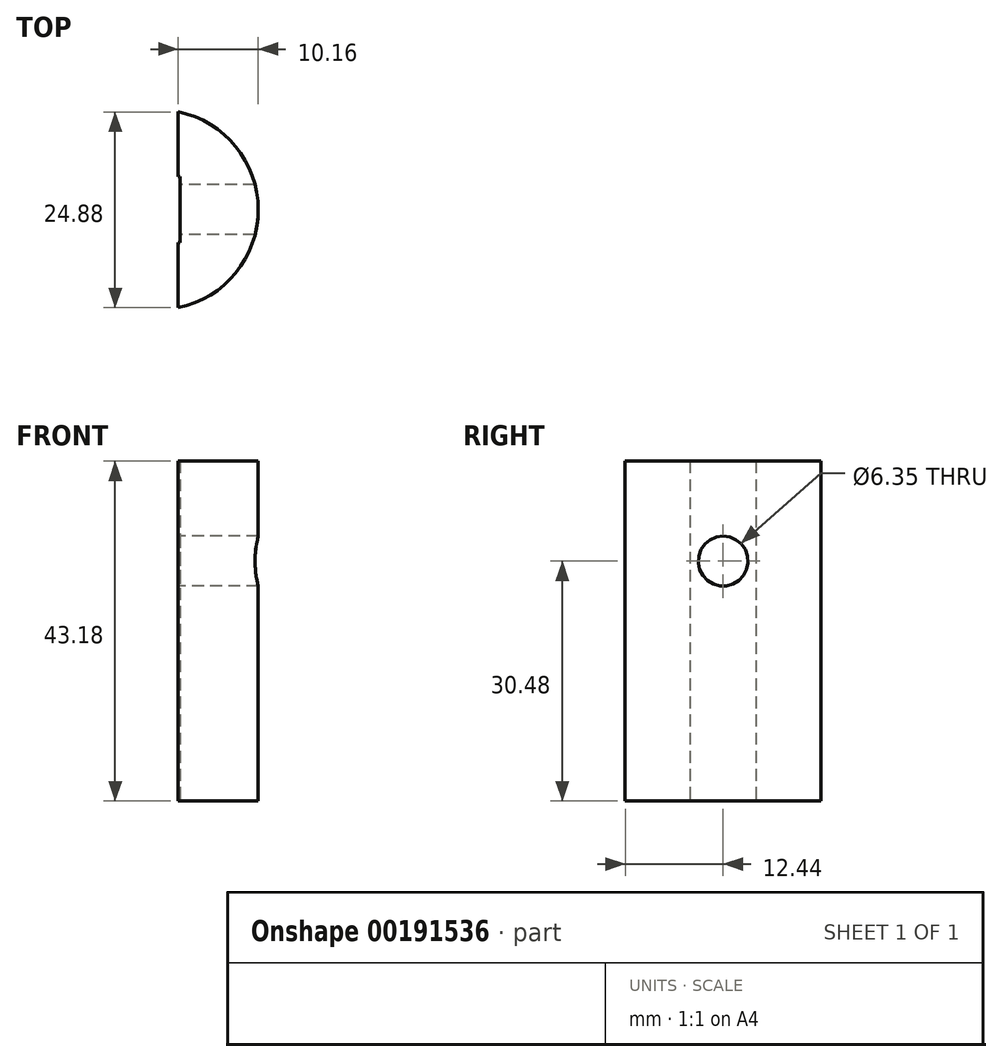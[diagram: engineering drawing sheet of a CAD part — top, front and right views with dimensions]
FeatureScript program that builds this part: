
annotation { "Feature Type Name" : "Feature", "Feature Type Description" : "" }
export const myFeature = defineFeature(function(context is Context, id is Id, definition is map)
    precondition{}
    {
        {
            var Q0;
            Q0=qCreatedBy(makeId("Top.planeOp"),FACE);
            var sketch = newSketch(context, id + "F0", { "sketchPlane" : qUnion([Q0])});
            skCircle(sketch, "E0", {"center": v(0, 0) * mm, "radius": 12.7 * mm});
            skLineSegment(sketch, "E1", {"start": v(0, -12.7) * mm, "end": v(0, 12.7) * mm});
            skLineSegment(sketch, "E2", {"start": v(2.54, -12.44) * mm, "end": v(2.54, 12.44) * mm});
            skLineSegment(sketch, "E3.bottom", {"start": v(2.8, -4.2) * mm, "end": v(2.29, -4.2) * mm});
            skLineSegment(sketch, "E3.top", {"start": v(2.8, 4.2) * mm, "end": v(2.29, 4.2) * mm});
            skLineSegment(sketch, "E3.left", {"start": v(2.8, -4.2) * mm, "end": v(2.8, 4.2) * mm});
            skLineSegment(sketch, "E3.right", {"start": v(2.29, -4.2) * mm, "end": v(2.29, 4.2) * mm});
            skPoint(sketch, "E3.middle", {"position": v(2.54, 0) * mm});
            skSolve(sketch);
        }
        {
            var Q0;
            {var subQ11=sQuery(id+"F0.wireOp",EDGE,"E3.left");Q0=makeQuery(id+"F0.imprint","IMPRINT",FACE,{"disambiguationData":[TD([[makeQuery(id+"F0.imprint","IMPRINT",EDGE,{"derivedFrom":subQ11}),-1.0]])]});}
            extrude(context, id + "F1", {"entities" : qUnion([Q0]), "depth" : 43.18 * mm});
        }
        {
            var Q0;
            Q0=qCreatedBy(makeId("Right.planeOp"),FACE);
            var sketch = newSketch(context, id + "F2", { "sketchPlane" : qUnion([Q0])});
            skLineSegment(sketch, "E4.0", {"start": v(-4.2, 43.18) * mm, "end": v(4.2, 43.18) * mm});
            skPoint(sketch, "E5", {"position": v(0, 30.48) * mm});
            skPoint(sketch, "E5.positionSnap0", {"position": v(0, 43.18) * mm});
            skSolve(sketch);
        }
        {
            var Q0;
            Q0=sQuery(id+"F2.wireOp",VERTEX,"E5");
            var Q1;
            Q1=makeQuery(id+"F1.opExtrude","SWEPT_BODY",BODY,{"disambiguationData":[OSD([sQuery(id+"F0.wireOp",EDGE,"E0"),sQuery(id+"F0.wireOp",EDGE,"E2"),sQuery(id+"F0.wireOp",EDGE,"E3.bottom"),sQuery(id+"F0.wireOp",EDGE,"E3.top"),sQuery(id+"F0.wireOp",EDGE,"E3.left")])]});
            hole(context, id + "F3", {"style" : HoleStyle.SIMPLE, "endStyle" : HoleEndStyle.THROUGH, "oppositeDirection" : true, "holeDiameter" : 6.35 * mm, "startFromSketch" : true, "locations" : qUnion([Q0]), "scope" : qUnion([Q1]), "isTappedThrough" : true});
        }
    });
